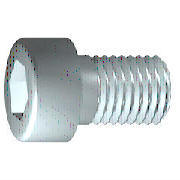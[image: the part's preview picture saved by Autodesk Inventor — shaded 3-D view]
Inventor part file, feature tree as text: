
AUTODESK INVENTOR PART (.ipt)
format: ipt  version: 2016 (Build 200138000, 138)  size: 197,120 bytes
history: native  units: mm (DEFAULTED — no unit token found)
features: sketch x2, extrude x1, plane x1, fillet x1
ambient origin geometry x7: Origin, YZ Plane, XY Plane, X Axis, Y Axis, Z Axis, Center Point
bodies: Solid1 (feature_tree), Body (feature_tree)
feature tree (5):
  extrude  "Slot"  Depth=3.0mm
  plane  "Work Plane1"
  fillet  "Fillet2"  Radius=3.0mm
  sketch  "Sketch1"  dims[d1=8.75mm d2=0.306825mm d3=3.0mm]
  sketch  "Sketch2"  dims[d4=1.3mm d5=60.0deg d6=3.0mm d7=3.0mm d8=2.886751mm d9=5.5mm d10=90.0deg d11=10.0mm d12=0.0mm d13=8.75mm d14=0.0mm d15=0.306725mm d16=0.306725mm d17=0.3mm d19=0.0mm d26=10.0mm d27=45.0deg d28=0.0mm d29=0.0mm d30=0.1mm]
